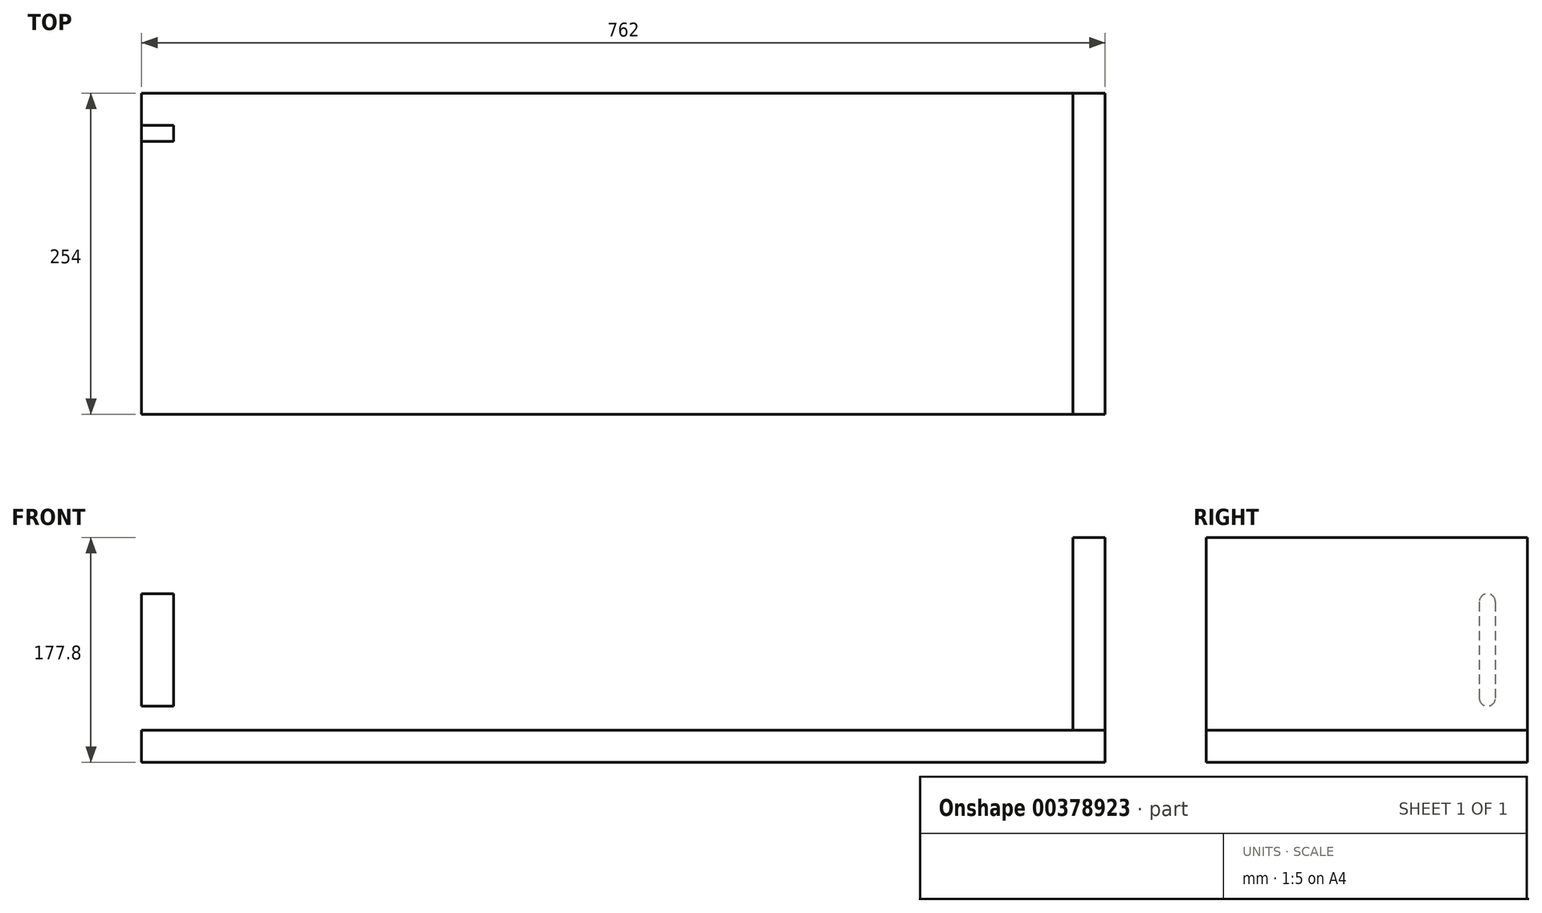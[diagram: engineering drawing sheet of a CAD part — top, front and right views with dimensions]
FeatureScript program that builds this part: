
annotation { "Feature Type Name" : "Feature", "Feature Type Description" : "" }
export const myFeature = defineFeature(function(context is Context, id is Id, definition is map)
    precondition{}
    {
        {
            var Q0;
            Q0=qCreatedBy(makeId("Top.planeOp"),FACE);
            var sketch = newSketch(context, id + "F0", { "sketchPlane" : qUnion([Q0])});
            skLineSegment(sketch, "E0.bottom", {"start": v(381, 127) * mm, "end": v(-381, 127) * mm});
            skLineSegment(sketch, "E0.top", {"start": v(381, -127) * mm, "end": v(-381, -127) * mm});
            skLineSegment(sketch, "E0.left", {"start": v(381, 127) * mm, "end": v(381, -127) * mm});
            skLineSegment(sketch, "E0.right", {"start": v(-381, 127) * mm, "end": v(-381, -127) * mm});
            skPoint(sketch, "E0.middle", {"position": v(0, 0) * mm});
            skSolve(sketch);
        }
        {
            var Q0;
            Q0=makeQuery(id+"F0.imprint","IMPRINT",FACE,{"disambiguationData":[TD([[makeQuery(id+"F0.imprint","IMPRINT",EDGE,{"derivedFrom":sQuery(id+"F0.wireOp",EDGE,"E0.bottom")}),1.0]])]});
            extrude(context, id + "F1", {"entities" : qUnion([Q0]), "depth" : 25.4 * mm});
        }
        {
            var Q0;
            Q0=makeQuery(id+"F1.opExtrude","CAP_FACE",FACE,{"disambiguationData":[OSD([sQuery(id+"F0.wireOp",EDGE,"E0.bottom"),sQuery(id+"F0.wireOp",EDGE,"E0.top"),sQuery(id+"F0.wireOp",EDGE,"E0.left"),sQuery(id+"F0.wireOp",EDGE,"E0.right")])],"isStart":false});
            var sketch = newSketch(context, id + "F2", { "sketchPlane" : qUnion([Q0])});
            skLineSegment(sketch, "E1.bottom", {"start": v(-381, 127) * mm, "end": v(-355.6, 127) * mm});
            skLineSegment(sketch, "E1.top", {"start": v(-381, -127) * mm, "end": v(-355.6, -127) * mm});
            skLineSegment(sketch, "E1.left", {"start": v(-381, 127) * mm, "end": v(-381, -127) * mm});
            skLineSegment(sketch, "E1.right", {"start": v(-355.6, 127) * mm, "end": v(-355.6, -127) * mm});
            skLineSegment(sketch, "E2", {"start": v(0, -127) * mm, "end": v(0, 127) * mm, "construction": true});
            skSolve(sketch);
        }
        {
            var Q0;
            Q0=makeQuery(id+"F2.imprint","IMPRINT",FACE,{"disambiguationData":[TD([[makeQuery(id+"F2.imprint","IMPRINT",EDGE,{"derivedFrom":sQuery(id+"F2.wireOp",EDGE,"E1.bottom")}),1.0]])]});
            extrude(context, id + "F3", {"entities" : qUnion([Q0]), "depth" : 152.4 * mm});
        }
        {
            var Q0;
            Q0=makeQuery(id+"F3.opExtrude","SWEPT_BODY",BODY,{"disambiguationData":[OSD([sQuery(id+"F2.wireOp",EDGE,"E1.bottom"),sQuery(id+"F2.wireOp",EDGE,"E1.top"),sQuery(id+"F2.wireOp",EDGE,"E1.left"),sQuery(id+"F2.wireOp",EDGE,"E1.right")])]});
            var Q1;
            Q1=qCreatedBy(makeId("Right.planeOp"),FACE);
            mirror(context, id + "F4", {"entities" : qUnion([Q0]), "mirrorPlane" : qUnion([Q1])});
        }
        {
            var Q0;
            Q0=makeQuery(id+"F3.opExtrude","SWEPT_FACE",FACE,{"disambiguationData":[OSD([sQuery(id+"F2.wireOp",EDGE,"E1.left")])]});
            var sketch = newSketch(context, id + "F5", { "sketchPlane" : qUnion([Q0])});
            skSolve(sketch);
        }
        {
            var Q0;
            {var subQ0=sQuery(id+"F2.wireOp",EDGE,"E1.left");Q0=makeQuery(id+"F5.imprint","IMPRINT",FACE,{"disambiguationData":[TD([[makeQuery(id+"F5.imprint","IMPRINT",EDGE,{"derivedFrom":makeQuery(id+"F3.opExtrude","CAP_EDGE",EDGE,{"disambiguationData":[OSD([subQ0])],"isStart":true})}),1.0]])]});}
            var sketch = newSketch(context, id + "F6", { "sketchPlane" : qUnion([Q0])});
            skLineSegment(sketch, "E3", {"start": v(-95.25, 127) * mm, "end": v(-95.25, 50.8) * mm, "construction": true});
            skArc(sketch, "E4.0.startCap", {"start": v(-101.6, 127) * mm, "mid": v(-95.25, 133.35) * mm, "end": v(-88.9, 127) * mm});
            skArc(sketch, "E4.0.endCap", {"start": v(-88.9, 50.8) * mm, "mid": v(-95.25, 44.45) * mm, "end": v(-101.6, 50.8) * mm});
            skLineSegment(sketch, "E4.0.left", {"start": v(-88.9, 127) * mm, "end": v(-88.9, 50.8) * mm});
            skLineSegment(sketch, "E4.0.right", {"start": v(-101.6, 127) * mm, "end": v(-101.6, 50.8) * mm});
            skSolve(sketch);
        }
        {
            var Q0;
            Q0=makeQuery(id+"F6.imprint","IMPRINT",FACE,{"disambiguationData":[TD([[makeQuery(id+"F6.imprint","IMPRINT",EDGE,{"derivedFrom":sQuery(id+"F6.wireOp",EDGE,"E4.0.startCap")}),-1.0]])]});
            extrude(context, id + "F7", {"entities" : qUnion([Q0]), "operationType" : NewBodyOperationType.REMOVE, "oppositeDirection" : true, "depth" : 25.4 * mm});
        }
    });
